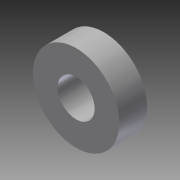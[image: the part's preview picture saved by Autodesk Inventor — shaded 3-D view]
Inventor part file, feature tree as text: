
AUTODESK INVENTOR PART (.ipt)
format: ipt  version: 2013 (Build 170138000, 138)  size: 78,848 bytes
history: native  units: in
note: dims shown in document units (in); Inventor stores cm internally (conversion verified against a paired STEP export)
features: extrude x1, sketch x1
ambient origin geometry x8: Origin, YZ Plane, XZ Plane, XY Plane, X Axis, Y Axis, Z Axis, Center Point
bodies: Solid1 (feature_tree)
feature tree (2):
  extrude  "Extrusion1"  Depth=0.375in
  sketch  "Sketch1"  dims[d0=0.875in d2=0.375in d3=0.281in d4=0.0in]
